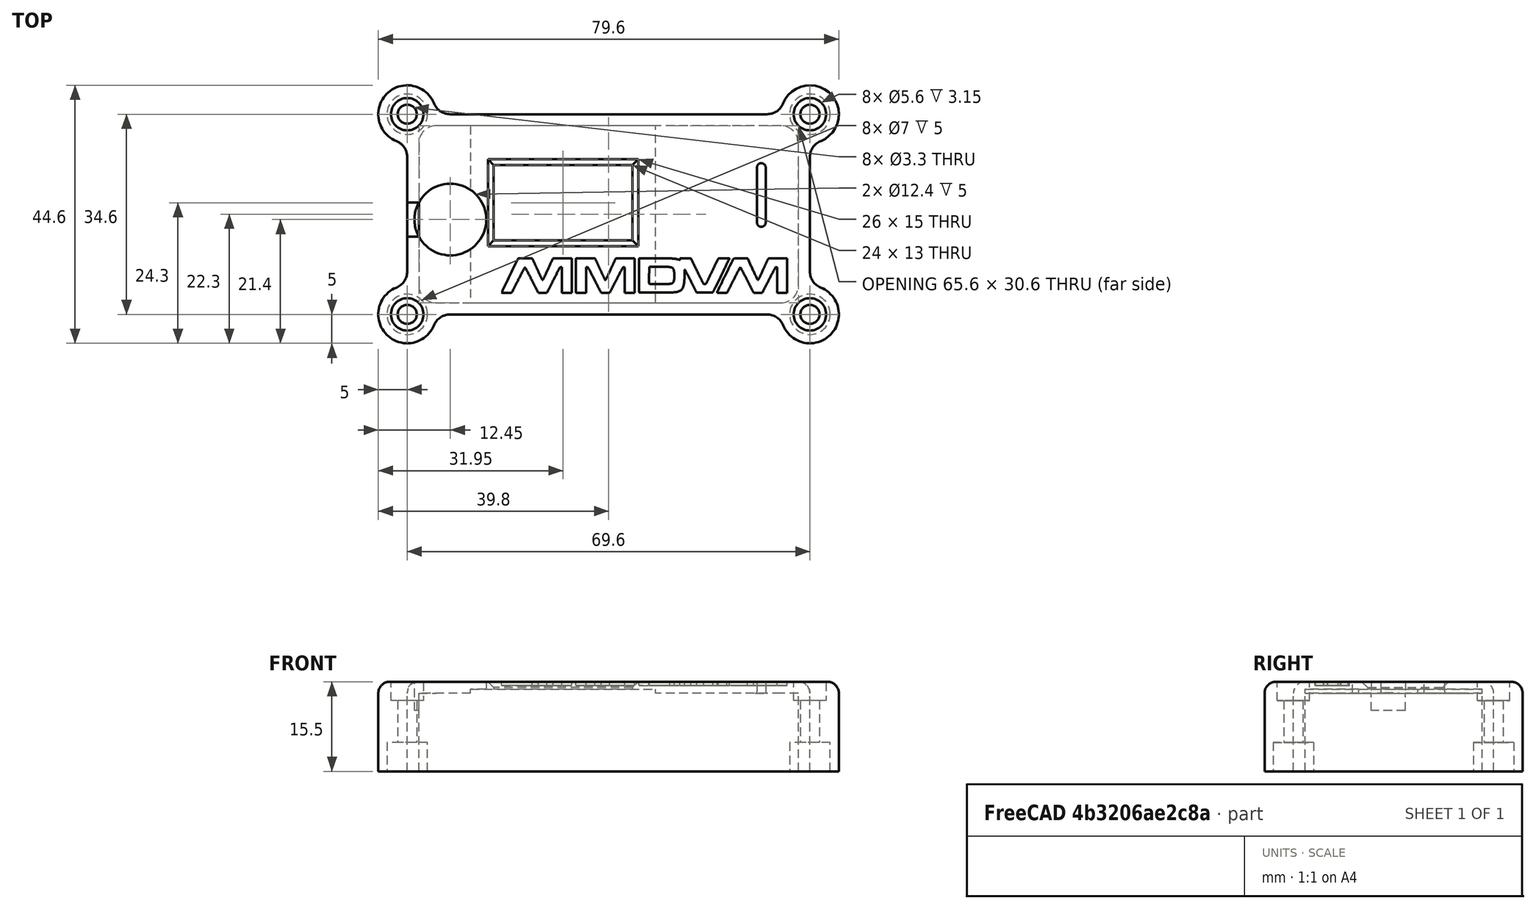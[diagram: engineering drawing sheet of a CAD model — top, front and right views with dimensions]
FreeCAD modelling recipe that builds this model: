
FCSTD DOCUMENT  (FreeCAD 0.18R13830 (Git))
Label: MMDVM_HS_Top-PCB-v1.2
License: CreativeCommons Attribution-NonCommercial-ShareAlike
LicenseURL: http://creativecommons.org/licenses/by-nc-sa/4.0/
objects: Sketcher::SketchObject×10, PartDesign::Pocket×6, Part::Feature×5, PartDesign::Fillet×3, Part::Cut×2, PartDesign::Pad×1, PartDesign::Chamfer×1, PartDesign::Hole×1, PartDesign::Body×1, Part::MultiFuse×1, Part::FeaturePython×1, Part::Extrusion×1, Mesh::Feature×1
note: 41 computed .brp shape members not serialized (recipe doc carries the construction recipe); baked Part::Feature solids carry a one-line shape summary decoded from their .brp

FEATURE [Sketcher::SketchObject] Sketch
  MapMode = 5
  Support = -> [XY_Plane]
  sketch-geometry (24):
    g0: LineSegment [constr] StartX=-32.5 StartY=15 StartZ=0 EndX=32.5 EndY=15 EndZ=0
    g1: LineSegment [constr] StartX=32.5 StartY=15 StartZ=0 EndX=32.5 EndY=-15 EndZ=0
    g2: LineSegment [constr] StartX=32.5 StartY=-15 StartZ=0 EndX=-32.5 EndY=-15 EndZ=0
    g3: LineSegment [constr] StartX=-32.5 StartY=-15 StartZ=0 EndX=-32.5 EndY=15 EndZ=0
    g4: LineSegment [constr] StartX=-29 StartY=11.5 StartZ=0 EndX=29 EndY=11.5 EndZ=0
    g5: LineSegment [constr] StartX=29 StartY=11.5 StartZ=0 EndX=29 EndY=-11.5 EndZ=0
    g6: LineSegment [constr] StartX=29 StartY=-11.5 StartZ=0 EndX=-29 EndY=-11.5 EndZ=0
    g7: LineSegment [constr] StartX=-29 StartY=-11.5 StartZ=0 EndX=-29 EndY=11.5 EndZ=0
    g8: Circle CenterX=-29 CenterY=11.5 CenterZ=0 NormalX=0 NormalY=0 NormalZ=1 AngleXU=0 Radius=1.375
    g9: Circle CenterX=29 CenterY=11.5 CenterZ=0 NormalX=0 NormalY=0 NormalZ=1 AngleXU=0 Radius=1.375
    g10: Circle CenterX=29 CenterY=-11.5 CenterZ=0 NormalX=0 NormalY=0 NormalZ=1 AngleXU=0 Radius=1.375
    g11: Circle CenterX=-29 CenterY=-11.5 CenterZ=0 NormalX=0 NormalY=0 NormalZ=1 AngleXU=0 Radius=1.375
    g12: LineSegment [constr] StartX=-29.5 StartY=12 StartZ=0 EndX=29.5 EndY=12 EndZ=0
    g13: LineSegment [constr] StartX=29.5 StartY=12 StartZ=0 EndX=29.5 EndY=-12 EndZ=0
    g14: LineSegment [constr] StartX=29.5 StartY=-12 StartZ=0 EndX=-29.5 EndY=-12 EndZ=0
    g15: LineSegment [constr] StartX=-29.5 StartY=-12 StartZ=0 EndX=-29.5 EndY=12 EndZ=0
    g16: ArcOfCircle CenterX=-29.5 CenterY=12 CenterZ=0 NormalX=0 NormalY=0 NormalZ=1 AngleXU=0 Radius=3 StartAngle=1.5708 EndAngle=3.1416
    g17: ArcOfCircle CenterX=29.5 CenterY=12 CenterZ=0 NormalX=0 NormalY=0 NormalZ=1 AngleXU=0 Radius=3 StartAngle=1.42077e-07 EndAngle=1.5708
    g18: ArcOfCircle CenterX=29.5 CenterY=-12 CenterZ=0 NormalX=0 NormalY=0 NormalZ=1 AngleXU=0 Radius=3 StartAngle=4.71239 EndAngle=6.28319
    g19: ArcOfCircle CenterX=-29.5 CenterY=-12 CenterZ=0 NormalX=0 NormalY=0 NormalZ=1 AngleXU=0 Radius=3 StartAngle=3.14159 EndAngle=4.71239
    g20: LineSegment StartX=-29.5 StartY=15 StartZ=0 EndX=29.5 EndY=15 EndZ=0
    g21: LineSegment StartX=32.5 StartY=12 StartZ=0 EndX=32.5 EndY=-12 EndZ=0
    g22: LineSegment StartX=29.5 StartY=-15 StartZ=0 EndX=-29.5 EndY=-15 EndZ=0
    g23: LineSegment StartX=-32.5 StartY=-12 StartZ=0 EndX=-32.5 EndY=12 EndZ=0
  constraints (68):
    c: Coincident(g0,g1)
    c: Coincident(g1,g2)
    c: Coincident(g2,g3)
    c: Coincident(g3,g0)
    c: Horizontal(g0)
    c: Horizontal(g2)
    c: Vertical(g1)
    c: Vertical(g3)
    c: DistanceX(g0,g0) = 65
    c: DistanceY(g1,g1) = 30
    c: Symmetric(g0,g0,g-2)
    c: Symmetric(g0,g1,g-1)
    c: Coincident(g4,g5)
    c: Coincident(g5,g6)
    c: Coincident(g6,g7)
    c: Coincident(g7,g4)
    c: Horizontal(g4)
    c: Horizontal(g6)
    c: Vertical(g5)
    c: Vertical(g7)
    c: DistanceX(g4,g4) = 58
    c: DistanceY(g5,g5) = 23
    c: Symmetric(g4,g5,g-1)
    c: Symmetric(g4,g4,g-2)
    c: Coincident(g8,g4)
    c: Coincident(g9,g4)
    c: Coincident(g10,g5)
    c: Coincident(g11,g6)
    c: Radius(g11) = 1.375
    c: Radius(g8) = 1.375
    c: Radius(g9) = 1.375
    c: Radius(g10) = 1.375
    c: Coincident(g12,g13)
    c: Coincident(g13,g14)
    c: Coincident(g14,g15)
    c: Coincident(g15,g12)
    c: Horizontal(g12)
    c: Horizontal(g14)
    c: Vertical(g13)
    c: Vertical(g15)
    c: DistanceX(g4,g12) = 0.5
    c: DistanceY(g4,g12) = 0.5
    c: DistanceY(g13,g5) = 0.5
    c: DistanceX(g14,g6) = 0.5
    c: Coincident(g16,g12)
    c: Radius(g16) = 3
    c: Coincident(g17,g12)
    c: Radius(g17) = 3
    c: Coincident(g18,g13)
    c: Radius(g18) = 3
    c: Coincident(g19,g14)
    c: Radius(g19) = 3
    c: PointOnObject(g16,g0)
    c: PointOnObject(g17,g1)
    c: PointOnObject(g18,g2)
    c: PointOnObject(g19,g3)
    c: Coincident(g20,g16)
    c: Horizontal(g20)
    c: Coincident(g20,g17)
    c: Coincident(g21,g17)
    c: Vertical(g21)
    c: Coincident(g18,g21)
    c: Coincident(g22,g18)
    c: Horizontal(g22)
    c: Coincident(g19,g22)
    c: Coincident(g23,g19)
    c: Vertical(g23)
    c: Coincident(g23,g16)
FEATURE [Sketcher::SketchObject] Sketch001
  MapMode = 5
  Support = -> [XY_Plane]
  expr: Constraints[8] = Sketch.Constraints[8]
  expr: Constraints[41] = Sketch.Constraints[41]
  expr: Constraints[9] = Sketch.Constraints[9]
  expr: Constraints[45] = Sketch.Constraints[45]
  expr: Constraints[43] = Sketch.Constraints[43]
  expr: Constraints[42] = Sketch.Constraints[42]
  expr: Constraints[20] = Sketch.Constraints[20]
  expr: Constraints[21] = Sketch.Constraints[21]
  expr: Constraints[28] = Sketch.Constraints[28]
  expr: Constraints[29] = Sketch.Constraints[29]
  expr: Constraints[30] = Sketch.Constraints[30]
  expr: Constraints[40] = Sketch.Constraints[40]
  expr: Constraints[31] = Sketch.Constraints[31]
  expr: Constraints[47] = Sketch.Constraints[47]
  expr: Constraints[49] = Sketch.Constraints[49]
  expr: Constraints[51] = Sketch.Constraints[51]
  sketch-geometry (64):
    g0: LineSegment [constr] StartX=-32.5 StartY=15 StartZ=0 EndX=32.5 EndY=15 EndZ=0
    g1: LineSegment [constr] StartX=32.5 StartY=15 StartZ=0 EndX=32.5 EndY=-15 EndZ=0
    g2: LineSegment [constr] StartX=32.5 StartY=-15 StartZ=0 EndX=-32.5 EndY=-15 EndZ=0
    g3: LineSegment [constr] StartX=-32.5 StartY=-15 StartZ=0 EndX=-32.5 EndY=15 EndZ=0
    g4: LineSegment [constr] StartX=-29 StartY=11.5 StartZ=0 EndX=29 EndY=11.5 EndZ=0
    g5: LineSegment [constr] StartX=29 StartY=11.5 StartZ=0 EndX=29 EndY=-11.5 EndZ=0
    g6: LineSegment [constr] StartX=29 StartY=-11.5 StartZ=0 EndX=-29 EndY=-11.5 EndZ=0
    g7: LineSegment [constr] StartX=-29 StartY=-11.5 StartZ=0 EndX=-29 EndY=11.5 EndZ=0
    g8: Circle [constr] CenterX=-29 CenterY=11.5 CenterZ=0 NormalX=0 NormalY=0 NormalZ=1 AngleXU=0 Radius=1.375
    g9: Circle [constr] CenterX=29 CenterY=11.5 CenterZ=0 NormalX=0 NormalY=0 NormalZ=1 AngleXU=0 Radius=1.375
    g10: Circle [constr] CenterX=29 CenterY=-11.5 CenterZ=0 NormalX=0 NormalY=0 NormalZ=1 AngleXU=0 Radius=1.375
    g11: Circle [constr] CenterX=-29 CenterY=-11.5 CenterZ=0 NormalX=0 NormalY=0 NormalZ=1 AngleXU=0 Radius=1.375
    g12: LineSegment [constr] StartX=-29.5 StartY=12 StartZ=0 EndX=29.5 EndY=12 EndZ=0
    g13: LineSegment [constr] StartX=29.5 StartY=12 StartZ=0 EndX=29.5 EndY=-12 EndZ=0
    g14: LineSegment [constr] StartX=29.5 StartY=-12 StartZ=0 EndX=-29.5 EndY=-12 EndZ=0
    g15: LineSegment [constr] StartX=-29.5 StartY=-12 StartZ=0 EndX=-29.5 EndY=12 EndZ=0
    g16: ArcOfCircle [constr] CenterX=-29.5 CenterY=12 CenterZ=0 NormalX=0 NormalY=0 NormalZ=1 AngleXU=0 Radius=3 StartAngle=1.5708 EndAngle=3.14159
    g17: ArcOfCircle [constr] CenterX=29.5 CenterY=12 CenterZ=0 NormalX=0 NormalY=0 NormalZ=1 AngleXU=0 Radius=3 StartAngle=2.8425e-08 EndAngle=1.5708
    g18: ArcOfCircle [constr] CenterX=29.5 CenterY=-12 CenterZ=0 NormalX=0 NormalY=0 NormalZ=1 AngleXU=0 Radius=3 StartAngle=4.71239 EndAngle=6.28319
    g19: ArcOfCircle [constr] CenterX=-29.5 CenterY=-12 CenterZ=0 NormalX=0 NormalY=0 NormalZ=1 AngleXU=0 Radius=3 StartAngle=3.14159 EndAngle=4.71239
    g20: LineSegment [constr] StartX=-29.5 StartY=15 StartZ=0 EndX=29.5 EndY=15 EndZ=0
    g21: LineSegment [constr] StartX=32.5 StartY=12 StartZ=0 EndX=32.5 EndY=-12 EndZ=0
    g22: LineSegment [constr] StartX=29.5 StartY=-15 StartZ=0 EndX=-29.5 EndY=-15 EndZ=0
    g23: LineSegment [constr] StartX=-32.5 StartY=-12 StartZ=0 EndX=-32.5 EndY=12 EndZ=0
    g24: ArcOfCircle [constr] CenterX=-29.5 CenterY=12 CenterZ=0 NormalX=0 NormalY=0 NormalZ=1 AngleXU=0 Radius=3.3 StartAngle=1.5708 EndAngle=3.14159
    g25: ArcOfCircle [constr] CenterX=29.5 CenterY=12 CenterZ=0 NormalX=0 NormalY=0 NormalZ=1 AngleXU=0 Radius=3.3 StartAngle=-2.2e-10 EndAngle=1.5708
    g26: ArcOfCircle [constr] CenterX=29.5 CenterY=-12 CenterZ=0 NormalX=0 NormalY=0 NormalZ=1 AngleXU=0 Radius=3.3 StartAngle=4.71239 EndAngle=6.28319
    g27: ArcOfCircle [constr] CenterX=-29.5 CenterY=-12 CenterZ=0 NormalX=0 NormalY=0 NormalZ=1 AngleXU=0 Radius=3.3 StartAngle=3.14159 EndAngle=4.71239
    g28: LineSegment [constr] StartX=-32.8 StartY=12 StartZ=0 EndX=-32.8 EndY=-12 EndZ=0
    g29: LineSegment [constr] StartX=-29.5 StartY=15.3 StartZ=0 EndX=29.5 EndY=15.3 EndZ=0
    g30: LineSegment [constr] StartX=32.8 StartY=12 StartZ=0 EndX=32.8 EndY=-12 EndZ=0
    g31: LineSegment [constr] StartX=29.5 StartY=-15.3 StartZ=0 EndX=-29.5 EndY=-15.3 EndZ=0
    g32: LineSegment [constr] StartX=-34.8 StartY=17.3 StartZ=0 EndX=34.8 EndY=17.3 EndZ=0
    g33: LineSegment [constr] StartX=34.8 StartY=17.3 StartZ=0 EndX=34.8 EndY=-17.3 EndZ=0
    g34: LineSegment [constr] StartX=34.8 StartY=-17.3 StartZ=0 EndX=-34.8 EndY=-17.3 EndZ=0
    g35: LineSegment [constr] StartX=-34.8 StartY=-17.3 StartZ=0 EndX=-34.8 EndY=17.3 EndZ=0
    g36: Circle [constr] CenterX=34.8 CenterY=17.3 CenterZ=0 NormalX=0 NormalY=0 NormalZ=1 AngleXU=0 Radius=5
    g37: Circle [constr] CenterX=34.8 CenterY=-17.3 CenterZ=0 NormalX=0 NormalY=0 NormalZ=1 AngleXU=0 Radius=5
    g38: Circle [constr] CenterX=-34.8 CenterY=-17.3 CenterZ=0 NormalX=0 NormalY=0 NormalZ=1 AngleXU=0 Radius=5
    g39: Circle [constr] CenterX=-34.8 CenterY=17.3 CenterZ=0 NormalX=0 NormalY=0 NormalZ=1 AngleXU=0 Radius=5
    g40: Circle [constr] CenterX=27.3838 CenterY=20.3 CenterZ=0 NormalX=0 NormalY=0 NormalZ=1 AngleXU=0 Radius=3
    g41: Circle [constr] CenterX=-27.3838 CenterY=20.3 CenterZ=0 NormalX=0 NormalY=0 NormalZ=1 AngleXU=0 Radius=3
    g42: Circle [constr] CenterX=-37.8 CenterY=9.8838 CenterZ=0 NormalX=0 NormalY=0 NormalZ=1 AngleXU=0 Radius=3
    g43: Circle [constr] CenterX=-37.8 CenterY=-9.8838 CenterZ=0 NormalX=0 NormalY=0 NormalZ=1 AngleXU=0 Radius=3
    g44: Circle [constr] CenterX=-27.3838 CenterY=-20.3 CenterZ=0 NormalX=0 NormalY=0 NormalZ=1 AngleXU=0 Radius=3
    g45: Circle [constr] CenterX=27.3838 CenterY=-20.3 CenterZ=0 NormalX=0 NormalY=0 NormalZ=1 AngleXU=0 Radius=3
    g46: Circle [constr] CenterX=37.8 CenterY=-9.8838 CenterZ=0 NormalX=0 NormalY=0 NormalZ=1 AngleXU=0 Radius=3
    g47: Circle [constr] CenterX=37.8 CenterY=9.8838 CenterZ=0 NormalX=0 NormalY=0 NormalZ=1 AngleXU=0 Radius=3
    g48: ArcOfCircle CenterX=34.8 CenterY=17.3 CenterZ=0 NormalX=0 NormalY=0 NormalZ=1 AngleXU=0 Radius=5 StartAngle=5.09679 EndAngle=9.04038
    g49: ArcOfCircle CenterX=27.3838 CenterY=20.3 CenterZ=0 NormalX=0 NormalY=0 NormalZ=1 AngleXU=0 Radius=3 StartAngle=4.71239 EndAngle=5.89879
    g50: ArcOfCircle CenterX=37.8 CenterY=9.8838 CenterZ=0 NormalX=0 NormalY=0 NormalZ=1 AngleXU=0 Radius=3 StartAngle=1.95519 EndAngle=3.14159
    g51: ArcOfCircle CenterX=37.8 CenterY=-9.8838 CenterZ=0 NormalX=0 NormalY=0 NormalZ=1 AngleXU=0 Radius=3 StartAngle=3.14159 EndAngle=4.32799
    g52: ArcOfCircle CenterX=34.8 CenterY=-17.3 CenterZ=0 NormalX=0 NormalY=0 NormalZ=1 AngleXU=0 Radius=5 StartAngle=3.52599 EndAngle=7.46958
    g53: ArcOfCircle CenterX=27.3838 CenterY=-20.3 CenterZ=0 NormalX=0 NormalY=0 NormalZ=1 AngleXU=0 Radius=3 StartAngle=0.384397 EndAngle=1.5708
    g54: ArcOfCircle CenterX=-27.3838 CenterY=-20.3 CenterZ=0 NormalX=0 NormalY=0 NormalZ=1 AngleXU=0 Radius=3 StartAngle=1.5708 EndAngle=2.7572
    g55: ArcOfCircle CenterX=-34.8 CenterY=-17.3 CenterZ=0 NormalX=0 NormalY=0 NormalZ=1 AngleXU=0 Radius=5 StartAngle=1.95519 EndAngle=5.89879
    g56: ArcOfCircle CenterX=-37.8 CenterY=-9.8838 CenterZ=0 NormalX=0 NormalY=0 NormalZ=1 AngleXU=0 Radius=3 StartAngle=5.09679 EndAngle=6.28319
    g57: ArcOfCircle CenterX=-37.8 CenterY=9.8838 CenterZ=0 NormalX=0 NormalY=0 NormalZ=1 AngleXU=0 Radius=3 StartAngle=6.28319 EndAngle=7.46958
    g58: ArcOfCircle CenterX=-34.8 CenterY=17.3 CenterZ=0 NormalX=0 NormalY=0 NormalZ=1 AngleXU=0 Radius=5 StartAngle=0.384397 EndAngle=4.32799
    g59: ArcOfCircle CenterX=-27.3838 CenterY=20.3 CenterZ=0 NormalX=0 NormalY=0 NormalZ=1 AngleXU=0 Radius=3 StartAngle=3.52599 EndAngle=4.71239
    g60: LineSegment StartX=-27.3838 StartY=17.3 StartZ=0 EndX=27.3838 EndY=17.3 EndZ=0
    g61: LineSegment StartX=34.8 StartY=9.8838 StartZ=0 EndX=34.8 EndY=-9.8838 EndZ=0
    g62: LineSegment StartX=27.3838 StartY=-17.3 StartZ=0 EndX=-27.3838 EndY=-17.3 EndZ=0
    g63: LineSegment StartX=-34.8 StartY=-9.8838 StartZ=0 EndX=-34.8 EndY=9.8838 EndZ=0
  constraints (184):
    c: Coincident(g0,g1)
    c: Coincident(g1,g2)
    c: Coincident(g2,g3)
    c: Coincident(g3,g0)
    c: Horizontal(g0)
    c: Horizontal(g2)
    c: Vertical(g1)
    c: Vertical(g3)
    c: DistanceX(g0,g0) = 65
    c: DistanceY(g1,g1) = 30
    c: Symmetric(g0,g0,g-2)
    c: Symmetric(g0,g1,g-1)
    c: Coincident(g4,g5)
    c: Coincident(g5,g6)
    c: Coincident(g6,g7)
    c: Coincident(g7,g4)
    c: Horizontal(g4)
    c: Horizontal(g6)
    c: Vertical(g5)
    c: Vertical(g7)
    c: DistanceX(g4,g4) = 58
    c: DistanceY(g5,g5) = 23
    c: Symmetric(g4,g5,g-1)
    c: Symmetric(g4,g4,g-2)
    c: Coincident(g8,g4)
    c: Coincident(g9,g4)
    c: Coincident(g10,g5)
    c: Coincident(g11,g6)
    c: Radius(g11) = 1.375
    c: Radius(g8) = 1.375
    c: Radius(g9) = 1.375
    c: Radius(g10) = 1.375
    c: Coincident(g12,g13)
    c: Coincident(g13,g14)
    c: Coincident(g14,g15)
    c: Coincident(g15,g12)
    c: Horizontal(g12)
    c: Horizontal(g14)
    c: Vertical(g13)
    c: Vertical(g15)
    c: DistanceX(g4,g12) = 0.5
    c: DistanceY(g4,g12) = 0.5
    c: DistanceY(g13,g5) = 0.5
    c: DistanceX(g14,g6) = 0.5
    c: Coincident(g16,g12)
    c: Radius(g16) = 3
    c: Coincident(g17,g12)
    c: Radius(g17) = 3
    c: Coincident(g18,g13)
    c: Radius(g18) = 3
    c: Coincident(g19,g14)
    c: Radius(g19) = 3
    c: PointOnObject(g16,g0)
    c: PointOnObject(g17,g1)
    c: PointOnObject(g18,g2)
    c: PointOnObject(g19,g3)
    c: Coincident(g20,g16)
    c: Horizontal(g20)
    c: Coincident(g20,g17)
    c: Coincident(g21,g17)
    c: Vertical(g21)
    c: Coincident(g18,g21)
    c: Coincident(g22,g18)
    c: Horizontal(g22)
    c: Coincident(g19,g22)
    c: Coincident(g23,g19)
    c: Vertical(g23)
    c: Coincident(g23,g16)
    c: Coincident(g24,g12)
    c: Radius(g24) = 3.3
    c: Coincident(g25,g12)
    c: Radius(g25) = 3.3
    c: Coincident(g26,g13)
    c: Radius(g26) = 3.3
    c: Coincident(g27,g14)
    c: Radius(g27) = 3.3
    c: Vertical(g28)
    c: DistanceX(g28,g2) = 0.3
    c: Coincident(g27,g28)
    c: Coincident(g28,g24)
    c: Horizontal(g29)
    c: DistanceY(g0,g29) = 0.3
    c: Coincident(g24,g29)
    c: Coincident(g25,g29)
    c: Vertical(g30)
    c: DistanceX(g0,g30) = 0.3
    c: Coincident(g25,g30)
    c: Coincident(g30,g26)
    c: Horizontal(g31)
    c: DistanceY(g31,g1) = 0.3
    c: Coincident(g31,g26)
    c: Coincident(g31,g27)
    c: Coincident(g32,g33)
    c: Coincident(g33,g34)
    c: Coincident(g34,g35)
    c: Coincident(g35,g32)
    c: Horizontal(g32)
    c: Horizontal(g34)
    c: Vertical(g33)
    c: Vertical(g35)
    c: DistanceY(g25,g32) = 2
    c: DistanceX(g25,g32) = 2
    c: DistanceY(g33,g26) = 2
    c: DistanceX(g34,g27) = 2
    c: Coincident(g36,g32)
    c: Coincident(g37,g33)
    c: Coincident(g38,g34)
    c: Coincident(g39,g32)
    c: Radius(g39) = 5
    c: Radius(g38) = 5
    c: Radius(g37) = 5
    c: Radius(g36) = 5
    c: Radius(g40) = 3
    c: Tangent(g40,g36)
    c: Tangent(g40,g32)
    c: Tangent(g47,g36)
    c: Radius(g47) = 3
    c: Tangent(g47,g33)
    c: Radius(g46) = 3
    c: Tangent(g46,g37)
    c: Tangent(g46,g33)
    c: Radius(g45) = 3
    c: Tangent(g45,g37)
    c: Tangent(g45,g34)
    c: Radius(g44) = 3
    c: Tangent(g44,g34)
    c: Tangent(g44,g38)
    c: Radius(g43) = 3
    c: Tangent(g43,g38)
    c: Tangent(g43,g35)
    c: Radius(g42) = 3
    c: Tangent(g42,g35)
    c: Tangent(g42,g39)
    c: Radius(g41) = 3
    c: Tangent(g41,g32)
    c: Tangent(g41,g39)
    c: Coincident(g48,g32)
    c: PointOnObject(g48,g36)
    c: Coincident(g49,g40)
    c: PointOnObject(g49,g40)
    c: Coincident(g50,g47)
    c: PointOnObject(g50,g47)
    c: Coincident(g51,g46)
    c: PointOnObject(g51,g46)
    c: Coincident(g52,g33)
    c: PointOnObject(g52,g37)
    c: Coincident(g53,g45)
    c: PointOnObject(g53,g45)
    c: Coincident(g54,g44)
    c: PointOnObject(g54,g44)
    c: Coincident(g55,g34)
    c: PointOnObject(g55,g38)
    c: Coincident(g56,g43)
    c: PointOnObject(g56,g43)
    c: Coincident(g57,g42)
    c: PointOnObject(g57,g42)
    c: Coincident(g58,g32)
    c: PointOnObject(g58,g39)
    c: Coincident(g59,g41)
    c: PointOnObject(g59,g41)
    c: Coincident(g49,g48)
    c: Coincident(g48,g50)
    c: Coincident(g51,g52)
    c: Coincident(g52,g53)
    c: Coincident(g54,g55)
    c: Coincident(g55,g56)
    c: Coincident(g57,g58)
    c: Coincident(g58,g59)
    c: PointOnObject(g60,g32)
    c: Horizontal(g60)
    c: PointOnObject(g61,g33)
    c: Vertical(g61)
    c: PointOnObject(g62,g34)
    c: Horizontal(g62)
    c: PointOnObject(g63,g35)
    c: Vertical(g63)
    c: Coincident(g59,g60)
    c: Coincident(g60,g49)
    c: Coincident(g50,g61)
    c: Coincident(g61,g51)
    c: Coincident(g53,g62)
    c: Coincident(g54,g62)
    c: Coincident(g56,g63)
    c: Coincident(g57,g63)
FEATURE [PartDesign::Pad] Pad
  Length = 15.5
  Length2 = 100
  Profile = -> Sketch001
  Type = 0
FEATURE [Sketcher::SketchObject] Sketch002
  ExternalGeometry = -> [Pad]
  MapMode = 5
  Placement = pos=(0,0,0) rot=(1,0,0;3.14159rad)
  Support = -> [Pad]
  sketch-geometry (4):
    g0: Circle CenterX=34.8 CenterY=17.3 CenterZ=0 NormalX=0 NormalY=0 NormalZ=1 AngleXU=0 Radius=3.5
    g1: Circle CenterX=34.8 CenterY=-17.3 CenterZ=0 NormalX=0 NormalY=0 NormalZ=1 AngleXU=0 Radius=3.5
    g2: Circle CenterX=-34.8 CenterY=-17.3 CenterZ=0 NormalX=0 NormalY=0 NormalZ=1 AngleXU=0 Radius=3.5
    g3: Circle CenterX=-34.8 CenterY=17.3 CenterZ=0 NormalX=0 NormalY=0 NormalZ=1 AngleXU=0 Radius=3.5
  constraints (8):
    c: Coincident(g0,g-3)
    c: Radius(g0) = 3.5
    c: Coincident(g1,g-6)
    c: Radius(g1) = 3.5
    c: Coincident(g2,g-5)
    c: Radius(g2) = 3.5
    c: Coincident(g3,g-4)
    c: Radius(g3) = 3.5
FEATURE [PartDesign::Pocket] Pocket
  BaseFeature = -> Pad
  Length = 5
  Length2 = 100
  Profile = -> Sketch002
  Type = 0
FEATURE [Sketcher::SketchObject] Sketch003
  MapMode = 5
  Placement = pos=(0,0,0) rot=(1,0,0;3.14159rad)
  Support = -> [Pocket]
  expr: Constraints[8] = Sketch.Constraints[8]
  expr: Constraints[39] = Sketch.Constraints[40]
  expr: Constraints[30] = Sketch.Constraints[31]
  expr: Constraints[27] = Sketch.Constraints[28]
  expr: Constraints[29] = Sketch.Constraints[30]
  expr: Constraints[28] = Sketch.Constraints[29]
  expr: Constraints[20] = -Sketch.Constraints[21]
  expr: Constraints[19] = Sketch.Constraints[20]
  expr: Constraints[42] = Sketch.Constraints[43]
  expr: Constraints[41] = -Sketch.Constraints[42]
  expr: Constraints[9] = -Sketch.Constraints[9]
  expr: Constraints[40] = -Sketch.Constraints[41]
  sketch-geometry (32):
    g0: LineSegment [constr] StartX=-32.5 StartY=-15 StartZ=0 EndX=32.5 EndY=-15 EndZ=0
    g1: LineSegment [constr] StartX=32.5 StartY=-15 StartZ=0 EndX=32.5 EndY=15 EndZ=0
    g2: LineSegment [constr] StartX=32.5 StartY=15 StartZ=0 EndX=-32.5 EndY=15 EndZ=0
    g3: LineSegment [constr] StartX=-32.5 StartY=15 StartZ=0 EndX=-32.5 EndY=-15 EndZ=0
    g4: LineSegment [constr] StartX=-29 StartY=-11.5 StartZ=0 EndX=29 EndY=-11.5 EndZ=0
    g5: LineSegment [constr] StartX=29 StartY=-11.5 StartZ=0 EndX=29 EndY=11.5 EndZ=0
    g6: LineSegment [constr] StartX=29 StartY=11.5 StartZ=0 EndX=-29 EndY=11.5 EndZ=0
    g7: LineSegment [constr] StartX=-29 StartY=11.5 StartZ=0 EndX=-29 EndY=-11.5 EndZ=0
    g8: Circle [constr] CenterX=-29 CenterY=-11.5 CenterZ=0 NormalX=0 NormalY=0 NormalZ=1 AngleXU=0 Radius=1.375
    g9: Circle [constr] CenterX=29 CenterY=-11.5 CenterZ=0 NormalX=0 NormalY=0 NormalZ=1 AngleXU=0 Radius=1.375
    g10: Circle [constr] CenterX=29 CenterY=11.5 CenterZ=0 NormalX=0 NormalY=0 NormalZ=1 AngleXU=0 Radius=1.375
    g11: Circle [constr] CenterX=-29 CenterY=11.5 CenterZ=0 NormalX=0 NormalY=0 NormalZ=1 AngleXU=0 Radius=1.375
    g12: LineSegment [constr] StartX=-29.5 StartY=-12 StartZ=0 EndX=29.5 EndY=-12 EndZ=0
    g13: LineSegment [constr] StartX=29.5 StartY=-12 StartZ=0 EndX=29.5 EndY=12 EndZ=0
    g14: LineSegment [constr] StartX=29.5 StartY=12 StartZ=0 EndX=-29.5 EndY=12 EndZ=0
    g15: LineSegment [constr] StartX=-29.5 StartY=12 StartZ=0 EndX=-29.5 EndY=-12 EndZ=0
    g16: LineSegment [constr] StartX=-29.5121 StartY=-15 StartZ=0 EndX=29.5 EndY=-15 EndZ=0
    g17: LineSegment [constr] StartX=32.5 StartY=-12 StartZ=0 EndX=32.5 EndY=12 EndZ=0
    g18: LineSegment [constr] StartX=29.5 StartY=15 StartZ=0 EndX=-29.5121 EndY=15 EndZ=0
    g19: LineSegment [constr] StartX=-32.5 StartY=12 StartZ=0 EndX=-32.5 EndY=-12 EndZ=0
    g20: ArcOfCircle [constr] CenterX=-29.5 CenterY=12 CenterZ=0 NormalX=0 NormalY=0 NormalZ=1 AngleXU=0 Radius=3.00002 StartAngle=1.57483 EndAngle=3.1416
    g21: ArcOfCircle [constr] CenterX=29.5 CenterY=12 CenterZ=0 NormalX=0 NormalY=0 NormalZ=1 AngleXU=0 Radius=3 StartAngle=6.28318 EndAngle=7.85399
    g22: ArcOfCircle [constr] CenterX=29.5 CenterY=-12 CenterZ=0 NormalX=0 NormalY=0 NormalZ=1 AngleXU=0 Radius=3 StartAngle=4.71238 EndAngle=6.28319
    g23: ArcOfCircle [constr] CenterX=-29.5 CenterY=-12 CenterZ=0 NormalX=0 NormalY=0 NormalZ=1 AngleXU=0 Radius=3.00002 StartAngle=3.14159 EndAngle=4.70836
    g24: LineSegment StartX=-29.8 StartY=15.3 StartZ=0 EndX=29.8 EndY=15.3 EndZ=0
    g25: LineSegment StartX=32.8 StartY=12.3 StartZ=0 EndX=32.8 EndY=-12.3 EndZ=0
    g26: LineSegment StartX=29.8 StartY=-15.3 StartZ=0 EndX=-29.8 EndY=-15.3 EndZ=0
    g27: LineSegment StartX=-32.8 StartY=-12.3 StartZ=0 EndX=-32.8 EndY=12.3 EndZ=0
    g28: ArcOfCircle CenterX=29.8 CenterY=12.3 CenterZ=0 NormalX=0 NormalY=0 NormalZ=1 AngleXU=0 Radius=3 StartAngle=0 EndAngle=1.5708
    g29: ArcOfCircle CenterX=29.8 CenterY=-12.3 CenterZ=0 NormalX=0 NormalY=0 NormalZ=1 AngleXU=0 Radius=3 StartAngle=4.71239 EndAngle=6.28319
    g30: ArcOfCircle CenterX=-29.8 CenterY=-12.3 CenterZ=0 NormalX=0 NormalY=0 NormalZ=1 AngleXU=0 Radius=3 StartAngle=3.14159 EndAngle=4.71239
    g31: ArcOfCircle CenterX=-29.8 CenterY=12.3 CenterZ=0 NormalX=0 NormalY=0 NormalZ=1 AngleXU=0 Radius=3 StartAngle=1.5708 EndAngle=3.14159
  constraints (83):
    c: Coincident(g0,g1)
    c: Coincident(g1,g2)
    c: Coincident(g2,g3)
    c: Coincident(g3,g0)
    c: Horizontal(g0)
    c: Horizontal(g2)
    c: Vertical(g1)
    c: Vertical(g3)
    c: DistanceX(g0,g0) = 65
    c: DistanceY(g1,g1) = -30
    c: Symmetric(g0,g0,g-2)
    c: Symmetric(g0,g1,g-1)
    c: Coincident(g4,g5)
    c: Coincident(g5,g6)
    c: Coincident(g6,g7)
    c: Horizontal(g4)
    c: Horizontal(g6)
    c: Vertical(g5)
    c: Vertical(g7)
    c: DistanceX(g4,g4) = 58
    c: DistanceY(g5,g5) = -23
    c: Symmetric(g4,g5,g-1)
    c: Symmetric(g4,g4,g-2)
    c: Coincident(g8,g4)
    c: Coincident(g9,g4)
    c: Coincident(g10,g5)
    c: Coincident(g11,g6)
    c: Radius(g11) = 1.375
    c: Radius(g8) = 1.375
    c: Radius(g9) = 1.375
    c: Radius(g10) = 1.375
    c: Coincident(g12,g13)
    c: Coincident(g13,g14)
    c: Coincident(g14,g15)
    c: Coincident(g15,g12)
    c: Horizontal(g12)
    c: Horizontal(g14)
    c: Vertical(g13)
    c: Vertical(g15)
    c: DistanceX(g4,g12) = 0.5
    c: DistanceY(g4,g12) = -0.5
    c: DistanceY(g13,g5) = -0.5
    c: DistanceX(g14,g6) = 0.5
    c: PointOnObject(g16,g0)
    c: PointOnObject(g17,g1)
    c: PointOnObject(g18,g2)
    c: PointOnObject(g19,g3)
    c: Horizontal(g16)
    c: Vertical(g17)
    c: Horizontal(g18)
    c: Vertical(g19)
    c: Coincident(g20,g14)
    c: Coincident(g20,g18)
    c: Coincident(g20,g19)
    c: Coincident(g21,g13)
    c: Coincident(g21,g17)
    c: Coincident(g21,g18)
    c: Coincident(g22,g12)
    c: Coincident(g22,g16)
    c: Coincident(g22,g17)
    c: Coincident(g23,g12)
    c: Coincident(g23,g19)
    c: Coincident(g23,g16)
    c: Horizontal(g24)
    c: Horizontal(g26)
    c: Vertical(g25)
    c: Vertical(g27)
    c: Tangent(g24,g28) = 1.5708
    c: Tangent(g25,g28) = 1.5708
    c: Tangent(g25,g29) = 1.5708
    c: Tangent(g26,g29) = 1.5708
    c: Tangent(g26,g30) = 1.5708
    c: Tangent(g27,g30) = 1.5708
    c: Tangent(g27,g31) = 1.5708
    c: Tangent(g24,g31) = 1.5708
    c: Radius(g31) = 3
    c: Radius(g28) = 3
    c: Radius(g29) = 3
    c: Radius(g30) = 3
    c: DistanceY(g1,g24) = 0.3
    c: DistanceX(g17,g25) = 0.3
    c: DistanceY(g26,g16) = 0.3
    c: DistanceX(g27,g19) = 0.3
FEATURE [PartDesign::Pocket] Pocket001
  BaseFeature = -> Pocket
  Length = 13.5
  Length2 = 100
  Profile = -> Sketch003
  Type = 0
FEATURE [Sketcher::SketchObject] Sketch004
  ExternalGeometry = -> [Pocket001]
  MapMode = 5
  Placement = pos=(0,0,15.5) rot=(0,0,1;0rad)
  Support = -> [Pocket001]
  sketch-geometry (32):
    g0: LineSegment StartX=-27.3838 StartY=17.3 StartZ=0 EndX=-31.8 EndY=17.3 EndZ=0
    g1: LineSegment StartX=-34.8 StartY=9.8838 StartZ=0 EndX=-34.8 EndY=14.3 EndZ=0
    g2: Circle [constr] CenterX=-31.8 CenterY=14.3 CenterZ=0 NormalX=0 NormalY=0 NormalZ=1 AngleXU=0 Radius=3
    g3: ArcOfCircle CenterX=-31.8 CenterY=14.3 CenterZ=0 NormalX=0 NormalY=0 NormalZ=1 AngleXU=0 Radius=3 StartAngle=1.5708 EndAngle=3.14159
    g4: LineSegment StartX=-41.7809 StartY=24.2149 StartZ=0 EndX=-27.3838 EndY=24.2149 EndZ=0
    g5: LineSegment StartX=-41.7809 StartY=9.8838 StartZ=0 EndX=-41.7809 EndY=24.2149 EndZ=0
    g6: LineSegment StartX=-27.3838 StartY=24.2149 StartZ=0 EndX=-27.3838 EndY=17.3 EndZ=0
    g7: LineSegment StartX=-41.7809 StartY=9.8838 StartZ=0 EndX=-34.8 EndY=9.8838 EndZ=0
    g8: LineSegment StartX=27.3838 StartY=17.3 StartZ=0 EndX=31.8 EndY=17.3 EndZ=0
    g9: LineSegment StartX=34.8 StartY=9.8838 StartZ=0 EndX=34.8 EndY=14.3 EndZ=0
    g10: Circle [constr] CenterX=31.8 CenterY=14.3 CenterZ=0 NormalX=0 NormalY=0 NormalZ=1 AngleXU=0 Radius=3
    g11: ArcOfCircle CenterX=31.8 CenterY=14.3 CenterZ=0 NormalX=0 NormalY=0 NormalZ=1 AngleXU=0 Radius=3 StartAngle=4.4834e-08 EndAngle=1.5708
    g12: LineSegment StartX=41.7622 StartY=24.6512 StartZ=0 EndX=27.3838 EndY=24.6512 EndZ=0
    g13: LineSegment StartX=41.7622 StartY=9.8838 StartZ=0 EndX=41.7622 EndY=24.6512 EndZ=0
    g14: LineSegment StartX=27.3838 StartY=24.6512 StartZ=0 EndX=27.3838 EndY=17.3 EndZ=0
    g15: LineSegment StartX=41.7622 StartY=9.8838 StartZ=0 EndX=34.8 EndY=9.8838 EndZ=0
    g16: LineSegment StartX=-34.8 StartY=-9.8838 StartZ=0 EndX=-34.8 EndY=-14.3 EndZ=0
    g17: LineSegment StartX=-27.3838 StartY=-17.3 StartZ=0 EndX=-31.8 EndY=-17.3 EndZ=0
    g18: Circle [constr] CenterX=-31.8 CenterY=-14.3 CenterZ=0 NormalX=0 NormalY=0 NormalZ=1 AngleXU=0 Radius=3
    g19: ArcOfCircle CenterX=-31.8 CenterY=-14.3 CenterZ=0 NormalX=0 NormalY=0 NormalZ=1 AngleXU=0 Radius=3 StartAngle=3.14159 EndAngle=4.71239
    g20: LineSegment StartX=-27.3838 StartY=-24.2044 StartZ=0 EndX=-41.4724 EndY=-24.2044 EndZ=0
    g21: LineSegment StartX=-41.4724 StartY=-24.2044 StartZ=0 EndX=-41.4724 EndY=-9.8838 EndZ=0
    g22: LineSegment StartX=-41.4724 StartY=-9.8838 StartZ=0 EndX=-34.8 EndY=-9.8838 EndZ=0
    g23: LineSegment StartX=-27.3838 StartY=-24.2044 StartZ=0 EndX=-27.3838 EndY=-17.3 EndZ=0
    g24: LineSegment StartX=34.8 StartY=-9.8838 StartZ=0 EndX=34.8 EndY=-14.3 EndZ=0
    g25: LineSegment StartX=27.3838 StartY=-17.3 StartZ=0 EndX=31.8 EndY=-17.3 EndZ=0
    g26: Circle [constr] CenterX=31.8 CenterY=-14.3 CenterZ=0 NormalX=0 NormalY=0 NormalZ=1 AngleXU=0 Radius=3
    g27: ArcOfCircle CenterX=31.8 CenterY=-14.3 CenterZ=0 NormalX=0 NormalY=0 NormalZ=1 AngleXU=0 Radius=3 StartAngle=4.71239 EndAngle=6.28319
    g28: LineSegment StartX=41.5436 StartY=-23.6904 StartZ=0 EndX=27.3838 EndY=-23.6904 EndZ=0
    g29: LineSegment StartX=41.5436 StartY=-9.8838 StartZ=0 EndX=41.5436 EndY=-23.6904 EndZ=0
    g30: LineSegment StartX=41.5436 StartY=-9.8838 StartZ=0 EndX=34.8 EndY=-9.8838 EndZ=0
    g31: LineSegment StartX=27.3838 StartY=-23.6904 StartZ=0 EndX=27.3838 EndY=-17.3 EndZ=0
  constraints (88):
    c: PointOnObject(g0,g-3)
    c: Horizontal(g0)
    c: PointOnObject(g1,g-6)
    c: Vertical(g1)
    c: Radius(g2) = 3
    c: Tangent(g2,g0)
    c: Tangent(g2,g1)
    c: Coincident(g3,g2)
    c: PointOnObject(g3,g2)
    c: Coincident(g3,g1)
    c: Coincident(g3,g0)
    c: Coincident(g5,g4)
    c: Horizontal(g4)
    c: Vertical(g5)
    c: Coincident(g6,g4)
    c: Vertical(g6)
    c: Coincident(g7,g5)
    c: Horizontal(g7)
    c: Coincident(g7,g1)
    c: Coincident(g6,g0)
    c: PointOnObject(g8,g-3)
    c: Horizontal(g8)
    c: PointOnObject(g9,g-4)
    c: Vertical(g9)
    c: Radius(g10) = 3
    c: Tangent(g10,g8)
    c: Tangent(g10,g9)
    c: Coincident(g11,g10)
    c: PointOnObject(g11,g10)
    c: Coincident(g11,g8)
    c: Coincident(g11,g9)
    c: Coincident(g13,g12)
    c: Horizontal(g12)
    c: Vertical(g13)
    c: Coincident(g14,g12)
    c: Vertical(g14)
    c: Coincident(g15,g13)
    c: Horizontal(g15)
    c: Coincident(g15,g9)
    c: Coincident(g14,g8)
    c: PointOnObject(g16,g-6)
    c: Vertical(g16)
    c: PointOnObject(g17,g-5)
    c: Horizontal(g17)
    c: Radius(g18) = 3
    c: Tangent(g18,g16)
    c: Tangent(g18,g17)
    c: Coincident(g19,g18)
    c: PointOnObject(g19,g18)
    c: Coincident(g19,g17)
    c: Coincident(g19,g16)
    c: Coincident(g20,g21)
    c: Horizontal(g20)
    c: Vertical(g21)
    c: Coincident(g22,g21)
    c: Horizontal(g22)
    c: Coincident(g23,g20)
    c: Vertical(g23)
    c: Coincident(g23,g17)
    c: Coincident(g22,g16)
    c: PointOnObject(g24,g-4)
    c: Vertical(g24)
    c: PointOnObject(g25,g-5)
    c: Horizontal(g25)
    c: Radius(g26) = 3
    c: Tangent(g26,g24)
    c: Tangent(g26,g25)
    c: Coincident(g27,g26)
    c: PointOnObject(g27,g26)
    c: Coincident(g27,g24)
    c: Coincident(g27,g25)
    c: Coincident(g29,g28)
    c: Horizontal(g28)
    c: Vertical(g29)
    c: Coincident(g30,g29)
    c: Horizontal(g30)
    c: Coincident(g31,g28)
    c: Vertical(g31)
    c: Coincident(g31,g25)
    c: Coincident(g30,g24)
    c: Coincident(g0,g-3)
    c: Coincident(g1,g-6)
    c: Coincident(g-6,g16)
    c: Coincident(g17,g-5)
    c: Coincident(g-5,g25)
    c: Coincident(g-4,g24)
    c: Coincident(g9,g-4)
    c: Coincident(g8,g-3)
FEATURE [Sketcher::SketchObject] Sketch005
  ExternalGeometry = -> [Pocket001,Sketch]
  MapMode = 5
  Placement = pos=(0,0,15.5) rot=(0,0,1;0rad)
  Support = -> [Pocket001]
  sketch-geometry (10):
    g0: LineSegment [constr] StartX=-27.35 StartY=31.2328 StartZ=0 EndX=-27.35 EndY=-27.0552 EndZ=0
    g1: LineSegment [constr] StartX=-45.4064 StartY=-0.9 StartZ=0 EndX=40.4454 EndY=-0.9 EndZ=0
    g2: Circle [constr] CenterX=-27.35 CenterY=-0.9 CenterZ=0 NormalX=0 NormalY=0 NormalZ=1 AngleXU=0 Radius=6.2
    g3: LineSegment StartX=-19.85 StartY=8.5 StartZ=0 EndX=4.15 EndY=8.5 EndZ=0
    g4: LineSegment StartX=4.15 StartY=8.5 StartZ=0 EndX=4.15 EndY=-4.5 EndZ=0
    g5: LineSegment StartX=4.15 StartY=-4.5 StartZ=0 EndX=-19.85 EndY=-4.5 EndZ=0
    g6: LineSegment StartX=-19.85 StartY=-4.5 StartZ=0 EndX=-19.85 EndY=8.5 EndZ=0
    g7: LineSegment [constr] StartX=-29 StartY=24.9491 StartZ=0 EndX=-29 EndY=-20.674 EndZ=0
    g8: LineSegment [constr] StartX=-44.8443 StartY=11.5 StartZ=0 EndX=14.9752 EndY=11.5 EndZ=0
    g9: Circle CenterX=-27.35 CenterY=-0.9 CenterZ=0 NormalX=0 NormalY=0 NormalZ=1 AngleXU=0 Radius=6.2
  constraints (21):
    c: Coincident(g5,g6)
    c: Coincident(g3,g6)
    c: Coincident(g4,g5)
    c: Coincident(g3,g4)
    c: DistanceX(g3,g3) = 24
    c: DistanceY(g4,g4) = 13
    c: Vertical(g7)
    c: Horizontal(g8)
    c: PointOnObject(g-4,g8)
    c: PointOnObject(g-4,g7)
    c: PointOnObject(g2,g0)
    c: PointOnObject(g2,g1)
    c: DistanceX(g7,g0) = 1.65
    c: DistanceX(g7,g3) = 9.15
    c: DistanceY(g3,g-4) = 3
    c: DistanceY(g1,g8) = 12.4
    c: Vertical(g0)
    c: Horizontal(g1)
    c: Radius(g2) = 6.2
    c: Coincident(g9,g2)
    c: Radius(g9) = 6.2
FEATURE [PartDesign::Pocket] Pocket002
  BaseFeature = -> Pocket001
  Length = 5
  Length2 = 100
  Profile = -> Sketch005
  Type = 0
FEATURE [Sketcher::SketchObject] Sketch006
  ExternalGeometry = -> [Pocket002]
  MapMode = 5
  Placement = pos=(0,0,13.5) rot=(1,0,0;3.14159rad)
  Support = -> [Pocket002]
  sketch-geometry (4):
    g0: LineSegment StartX=-23.85 StartY=15.3 StartZ=0 EndX=8.15 EndY=15.3 EndZ=0
    g1: LineSegment StartX=8.15 StartY=15.3 StartZ=0 EndX=8.15 EndY=-15.3 EndZ=0
    g2: LineSegment StartX=8.15 StartY=-15.3 StartZ=0 EndX=-23.85 EndY=-15.3 EndZ=0
    g3: LineSegment StartX=-23.85 StartY=-15.3 StartZ=0 EndX=-23.85 EndY=15.3 EndZ=0
FEATURE [PartDesign::Pocket] Pocket003
  BaseFeature = -> Pocket002
  Length = 0.7
  Length2 = 100
  Profile = -> Sketch006
  Type = 0
FEATURE [PartDesign::Fillet] Fillet
  Base = -> Pocket003 [Edge38]
  BaseFeature = -> Pocket003
  Radius = 2
FEATURE [PartDesign::Chamfer] Chamfer
  Base = -> Fillet [Edge60,Edge61,Edge62,Edge63]
  BaseFeature = -> Fillet
  Size = 1
FEATURE [Sketcher::SketchObject] Sketch007
  MapMode = 5
  Placement = pos=(0,0,15.5) rot=(0,0,1;0rad)
  sketch-geometry (4):
    g0: Circle CenterX=34.8 CenterY=17.3 CenterZ=0 NormalX=0 NormalY=0 NormalZ=1 AngleXU=0 Radius=2.63102
    g1: Circle CenterX=-34.8 CenterY=17.3 CenterZ=0 NormalX=0 NormalY=0 NormalZ=1 AngleXU=0 Radius=2.66333
    g2: Circle CenterX=-34.8 CenterY=-17.3 CenterZ=0 NormalX=0 NormalY=0 NormalZ=1 AngleXU=0 Radius=2.82775
    g3: Circle CenterX=34.8 CenterY=-17.3 CenterZ=0 NormalX=0 NormalY=0 NormalZ=1 AngleXU=0 Radius=2.89107
FEATURE [PartDesign::Hole] Hole
  BaseFeature = -> Chamfer
  Depth = 20
  DepthType = 1
  Diameter = 3.3
  DrillPoint = 1
  DrillPointAngle = 118
  HoleCutCountersinkAngle = 90
  HoleCutDepth = 0
  HoleCutDiameter = 3
  HoleCutType = 0
  ModelActualThread = false
  Profile = -> Sketch007
  Tapered = false
  TaperedAngle = 90
  ThreadAngle = 60
  ThreadClass = 0
  ThreadCutOffInner = 0.0433013
  ThreadCutOffOuter = 0.0866025
  ThreadDirection = 0
  ThreadFit = 0
  ThreadPitch = 0.4
  ThreadSize = 3
  ThreadType = 1
  Threaded = false
FEATURE [Sketcher::SketchObject] Sketch008
  ExternalGeometry = -> [Hole]
  MapMode = 5
  Placement = pos=(0,0,15.5) rot=(0,0,1;0rad)
  Support = -> [Hole]
  sketch-geometry (4):
    g0: Circle CenterX=34.8 CenterY=17.3 CenterZ=0 NormalX=0 NormalY=0 NormalZ=1 AngleXU=0 Radius=2.8
    g1: Circle CenterX=34.8 CenterY=-17.3 CenterZ=0 NormalX=0 NormalY=0 NormalZ=1 AngleXU=0 Radius=2.8
    g2: Circle CenterX=-34.8 CenterY=-17.3 CenterZ=0 NormalX=0 NormalY=0 NormalZ=1 AngleXU=0 Radius=2.8
    g3: Circle CenterX=-34.8 CenterY=17.3 CenterZ=0 NormalX=0 NormalY=0 NormalZ=1 AngleXU=0 Radius=2.8
  constraints (7):
    c: Coincident(g0,g-5)
    c: Coincident(g1,g-8)
    c: Coincident(g3,g-6)
    c: Radius(g3) = 2.8
    c: Radius(g0) = 2.8
    c: Radius(g2) = 2.8
    c: Radius(g1) = 2.8
FEATURE [PartDesign::Pocket] Pocket004
  BaseFeature = -> Hole
  Length = 3.3
  Length2 = 100
  Profile = -> Sketch008
  Type = 0
FEATURE [PartDesign::Fillet] Fillet002
  Base = -> Pocket004 [Edge23,Edge22,Edge20,Edge21]
  BaseFeature = -> Pocket004
  Radius = 0.15
FEATURE [Sketcher::SketchObject] Sketch009
  MapMode = 5
  Placement = pos=(0,0,15.5) rot=(0,0,1;0rad)
  Support = -> [Fillet002]
  expr: Constraints[7] = Sketch.Constraints[9]
  expr: Constraints[40] = Sketch.Constraints[42]
  expr: Constraints[18] = Sketch.Constraints[20]
  expr: Constraints[19] = Sketch.Constraints[21]
  expr: Constraints[29] = Sketch.Constraints[31]
  expr: Constraints[27] = Sketch.Constraints[29]
  expr: Constraints[28] = Sketch.Constraints[30]
  expr: Constraints[26] = Sketch.Constraints[28]
  expr: Constraints[6] = Sketch.Constraints[8]
  expr: Constraints[38] = Sketch.Constraints[40]
  expr: Constraints[47] = Sketch.Constraints[49]
  expr: Constraints[39] = Sketch.Constraints[41]
  expr: Constraints[49] = Sketch.Constraints[51]
  expr: Constraints[45] = Sketch.Constraints[47]
  expr: Constraints[43] = Sketch.Constraints[45]
  expr: Constraints[41] = Sketch.Constraints[43]
  sketch-geometry (34):
    g0: LineSegment [constr] StartX=-32.5 StartY=15 StartZ=0 EndX=32.5 EndY=15 EndZ=0
    g1: LineSegment [constr] StartX=32.5 StartY=15 StartZ=0 EndX=32.5 EndY=-15 EndZ=0
    g2: LineSegment [constr] StartX=32.5 StartY=-15 StartZ=0 EndX=-32.5 EndY=-15 EndZ=0
    g3: LineSegment [constr] StartX=-32.5 StartY=-15 StartZ=0 EndX=-32.5 EndY=15 EndZ=0
    g4: LineSegment [constr] StartX=-29 StartY=11.5 StartZ=0 EndX=29 EndY=11.5 EndZ=0
    g5: LineSegment [constr] StartX=29 StartY=11.5 StartZ=0 EndX=29 EndY=-11.5 EndZ=0
    g6: LineSegment [constr] StartX=29 StartY=-11.5 StartZ=0 EndX=-29 EndY=-11.5 EndZ=0
    g7: LineSegment [constr] StartX=-29 StartY=-11.5 StartZ=0 EndX=-29 EndY=11.5 EndZ=0
    g8: Circle [constr] CenterX=-29 CenterY=11.5 CenterZ=0 NormalX=0 NormalY=0 NormalZ=1 AngleXU=0 Radius=1.375
    g9: Circle [constr] CenterX=29 CenterY=11.5 CenterZ=0 NormalX=0 NormalY=0 NormalZ=1 AngleXU=0 Radius=1.375
    g10: Circle [constr] CenterX=29 CenterY=-11.5 CenterZ=0 NormalX=0 NormalY=0 NormalZ=1 AngleXU=0 Radius=1.375
    g11: Circle [constr] CenterX=-29 CenterY=-11.5 CenterZ=0 NormalX=0 NormalY=0 NormalZ=1 AngleXU=0 Radius=1.375
    g12: LineSegment [constr] StartX=-29.5 StartY=12 StartZ=0 EndX=29.5 EndY=12 EndZ=0
    g13: LineSegment [constr] StartX=29.5 StartY=12 StartZ=0 EndX=29.5 EndY=-12 EndZ=0
    g14: LineSegment [constr] StartX=29.5 StartY=-12 StartZ=0 EndX=-29.5 EndY=-12 EndZ=0
    g15: LineSegment [constr] StartX=-29.5 StartY=-12 StartZ=0 EndX=-29.5 EndY=12 EndZ=0
    g16: ArcOfCircle [constr] CenterX=-29.5 CenterY=12 CenterZ=0 NormalX=0 NormalY=0 NormalZ=1 AngleXU=0 Radius=3 StartAngle=1.5708 EndAngle=3.14159
    g17: ArcOfCircle [constr] CenterX=29.5 CenterY=12 CenterZ=0 NormalX=0 NormalY=0 NormalZ=1 AngleXU=0 Radius=3 StartAngle=3.9602e-08 EndAngle=1.5708
    g18: ArcOfCircle [constr] CenterX=29.5 CenterY=-12 CenterZ=0 NormalX=0 NormalY=0 NormalZ=1 AngleXU=0 Radius=3 StartAngle=4.71239 EndAngle=6.28319
    g19: ArcOfCircle [constr] CenterX=-29.5 CenterY=-12 CenterZ=0 NormalX=0 NormalY=0 NormalZ=1 AngleXU=0 Radius=3 StartAngle=3.14159 EndAngle=4.71239
    g20: LineSegment [constr] StartX=-29.5 StartY=15 StartZ=0 EndX=29.5 EndY=15 EndZ=0
    g21: LineSegment [constr] StartX=32.5 StartY=12 StartZ=0 EndX=32.5 EndY=-12 EndZ=0
    g22: LineSegment [constr] StartX=29.5 StartY=-15 StartZ=0 EndX=-29.5 EndY=-15 EndZ=0
    g23: LineSegment [constr] StartX=-32.5 StartY=-12 StartZ=0 EndX=-32.5 EndY=12 EndZ=0
    g24: LineSegment [constr] StartX=26.4 StartY=27.403 StartZ=0 EndX=26.4 EndY=-26.3119 EndZ=0
    g25: ArcOfCircle CenterX=26.4 CenterY=8.09 CenterZ=0 NormalX=0 NormalY=0 NormalZ=1 AngleXU=0 Radius=0.75 StartAngle=0 EndAngle=3.14159
    g26: ArcOfCircle CenterX=26.4 CenterY=-1.41 CenterZ=0 NormalX=0 NormalY=0 NormalZ=1 AngleXU=0 Radius=0.75 StartAngle=3.14159 EndAngle=6.28319
    g27: LineSegment StartX=25.65 StartY=8.09 StartZ=0 EndX=25.65 EndY=-1.41 EndZ=0
    g28: LineSegment StartX=27.15 StartY=8.09 StartZ=0 EndX=27.15 EndY=-1.41 EndZ=0
    g29: LineSegment [constr] StartX=36.6897 StartY=3.34 StartZ=0 EndX=15.0074 EndY=3.34 EndZ=0
    g30: LineSegment [constr] StartX=25.4202 StartY=8.84 StartZ=0 EndX=27.4202 EndY=8.84 EndZ=0
    g31: LineSegment [constr] StartX=27.4202 StartY=8.84 StartZ=0 EndX=27.4202 EndY=-2.16 EndZ=0
    g32: LineSegment [constr] StartX=27.4202 StartY=-2.16 StartZ=0 EndX=25.4202 EndY=-2.16 EndZ=0
    g33: LineSegment [constr] StartX=25.4202 StartY=-2.16 StartZ=0 EndX=25.4202 EndY=8.84 EndZ=0
  constraints (91):
    c: Coincident(g0,g1)
    c: Coincident(g1,g2)
    c: Coincident(g2,g3)
    c: Coincident(g3,g0)
    c: Horizontal(g2)
    c: Vertical(g3)
    c: DistanceX(g0,g0) = 65
    c: DistanceY(g1,g1) = 30
    c: Symmetric(g0,g0,g-2)
    c: Symmetric(g0,g1,g-1)
    c: Coincident(g4,g5)
    c: Coincident(g5,g6)
    c: Coincident(g6,g7)
    c: Coincident(g7,g4)
    c: Horizontal(g4)
    c: Horizontal(g6)
    c: Vertical(g5)
    c: Vertical(g7)
    c: DistanceX(g4,g4) = 58
    c: DistanceY(g5,g5) = 23
    c: Symmetric(g4,g5,g-1)
    c: Symmetric(g4,g4,g-2)
    c: Coincident(g8,g4)
    c: Coincident(g9,g4)
    c: Coincident(g10,g5)
    c: Coincident(g11,g6)
    c: Radius(g11) = 1.375
    c: Radius(g8) = 1.375
    c: Radius(g9) = 1.375
    c: Radius(g10) = 1.375
    c: Coincident(g12,g13)
    c: Coincident(g13,g14)
    c: Coincident(g14,g15)
    c: Coincident(g15,g12)
    c: Horizontal(g12)
    c: Horizontal(g14)
    c: Vertical(g13)
    c: Vertical(g15)
    c: DistanceX(g4,g12) = 0.5
    c: DistanceY(g4,g12) = 0.5
    c: DistanceY(g13,g5) = 0.5
    c: DistanceX(g14,g6) = 0.5
    c: Coincident(g16,g12)
    c: Radius(g16) = 3
    c: Coincident(g17,g12)
    c: Radius(g17) = 3
    c: Coincident(g18,g13)
    c: Radius(g18) = 3
    c: Coincident(g19,g14)
    c: Radius(g19) = 3
    c: PointOnObject(g16,g0)
    c: PointOnObject(g17,g1)
    c: PointOnObject(g18,g2)
    c: PointOnObject(g19,g3)
    c: Coincident(g20,g16)
    c: Horizontal(g20)
    c: Coincident(g20,g17)
    c: Coincident(g21,g17)
    c: Vertical(g21)
    c: Coincident(g18,g21)
    c: Coincident(g22,g18)
    c: Horizontal(g22)
    c: Coincident(g19,g22)
    c: Coincident(g23,g19)
    c: Vertical(g23)
    c: Coincident(g23,g16)
    c: Vertical(g24)
    c: DistanceX(g24,g4) = 2.6
    c: Tangent(g25,g28) = 1.5708
    c: Tangent(g25,g27) = -1.5708
    c: Tangent(g27,g26) = -1.5708
    c: Tangent(g28,g26) = 1.5708
    c: Vertical(g27)
    c: Equal(g25,g26)
    c: PointOnObject(g25,g24)
    c: DistanceX(g26,g26) = 1.5
    c: Horizontal(g29)
    c: DistanceY(g29,g4) = 8.16
    c: Coincident(g30,g31)
    c: Coincident(g31,g32)
    c: Coincident(g32,g33)
    c: Coincident(g33,g30)
    c: Horizontal(g30)
    c: Horizontal(g32)
    c: Vertical(g31)
    c: Vertical(g33)
    c: DistanceY(g33,g33) = 11
    c: DistanceY(g29,g30) = 5.5
    c: DistanceX(g30,g30) = 2
    c: DistanceY(g26,g25) = 9.5
    c: Symmetric(g25,g26,g29)
FEATURE [PartDesign::Pocket] Pocket005
  BaseFeature = -> Fillet002
  Length = 5
  Length2 = 100
  Profile = -> Sketch009
  Type = 2
FEATURE [PartDesign::Fillet] Fillet003
  Base = -> Pocket005 [Edge22,Edge87]
  BaseFeature = -> Pocket005
  Radius = 0.3
FEATURE [PartDesign::Body] Body
  Group = -> [Sketch,Sketch001,Pad,Sketch002,Pocket,Sketch003,Pocket001,Sketch004,Sketch005,Pocket002,Sketch006,Pocket003,Fillet,Chamfer,Sketch007,Hole,Sketch008,Pocket004,Fillet002,Sketch009,Pocket005,Fillet003]
  Origin = -> Origin
  Tip = -> Fillet003
FEATURE [Part::Feature] path76
  shape: bbox 67.53 x 33.36 x 2e-07 mm, 1 faces, 0 solids (baked)
FEATURE [Part::Feature] path76001
  shape: bbox 56.51 x 33.36 x 2e-07 mm, 1 faces, 0 solids (baked)
FEATURE [Part::Feature] path76002
  shape: bbox 67.23 x 33.39 x 2e-07 mm, 1 faces, 0 solids (baked)
FEATURE [Part::Feature] path76003
  shape: bbox 86.8 x 33.05 x 2e-07 mm, 1 faces, 0 solids (baked)
FEATURE [Part::Feature] path76004
  shape: bbox 24.36 x 17.06 x 2e-07 mm, 1 faces, 0 solids (baked)
FEATURE [Part::Cut] Cut
  Base = -> path76003
  Tool = -> path76004
FEATURE [Part::MultiFuse] Fusion
  Shapes = -> [path76,path76001,path76002,Cut]
FEATURE [Part::FeaturePython] Scale001  # Draft clone (typed FeaturePython)
  Fuse = false
  Objects = -> [Fusion]
  Placement = pos=(-20,0,14.85) rot=(0,0,1;0rad)
  Scale = (0.18,0.18,0.18)
FEATURE [Part::Extrusion] Extrude001
  Base = -> Scale001
  Dir = (0,0,1)
  DirMode = 0
  FaceMakerClass = Part::FaceMakerBullseye
  LengthFwd = 5
  LengthRev = 0
  Solid = false
  Symmetric = false
FEATURE [Part::Cut] Cut001
  Base = -> Fillet003
  Tool = -> Extrude001
FEATURE [Mesh::Feature] Mesh  label="Cut001 (Meshed)"
